# Revit family: PL-PGS-048-WPx-R
name_source: partatom
category: HLS-Bauteile
units: mm (PartAtom-declared; Revit-internal decimal feet)

## family parameters
Arbeitsebenenbasiert = Nein
Beim Laden mit Abzugskörper schneiden = Nein
Bemaßung runder Anschluss = Durchmesser verwenden
Gemeinsam genutzt = Nein
Immer vertikal = Ja
Klassifizierung = Keine
Raumberechnungspunkt = Nein
Teiletyp = Normal

## types (1)
- PL-PGS-048-WPx-R
    Bauelement = 29.02.01.01
    Beschreibung = RLT-Gerät
    Classification.OmniClass.23.Description = Pre Fabricated Air Handling Units
    Classification.OmniClass.23.Number = 23-33 25 19
    DPWW = 25 mm  [stored 0.082021 ft]
    Family.Subcategory.Name = Air Handling Unit
    Hersteller = Hansa
    Höhe = 1865 mm  [stored 6.11877 ft]
    L1 = 785 mm
    L2 = 1640 mm  [stored 5.38058 ft]
    L3 = 785 mm
    Modell = PL-PGS-048-WPx-R
    RLT_Volumenstrom_max = 4800 m³/h
    Tiefe = 1280 mm  [stored 4.19948 ft]
    Vorgabe-Ansicht = 0 mm  [stored 0 ft]

note: [stored X ft] marks values corroborated as IEEE doubles in the binary element streams (Revit-internal decimal feet)

## geometry (parser evidence)
native form markers: Sweep x3
no freeform markers — native parametric forms only
